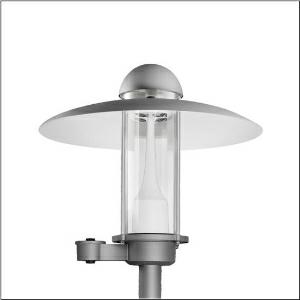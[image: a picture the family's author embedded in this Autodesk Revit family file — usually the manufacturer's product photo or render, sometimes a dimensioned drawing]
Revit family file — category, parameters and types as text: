
# Revit family: city-light_elegance_iq___st1_2a_5xa5265eu14h000022_aff6
name_source: partatom
category: Lighting Fixtures
units: mm (PartAtom-declared; Revit-internal decimal feet)

## family parameters
Cut with Voids When Loaded = No
Host = Face
Light Source = No
Part Type = Normal
Room Calculation Point = No
Round Connector Dimension = Use Diameter
Shared = No

## types (1)
- --- (1 x LED, 1460 lm, 10.7 W, 3000K)
    Apparent Load = 11 VA
    CIE Flux Codes = 22 62 94 98 100
    Color Rendering = 70
    Color Temperature = 3000K
    Default Elevation = 1800 mm
    Description = City-Light Elegance iQ, mast luminaire, Module 540 iQ-SR, primary light control with 3 zone facetted reflector, of plastic, silver coated, highly specular, structured, primary optical cover: cover, of PMMA, transparent, light distribution: ST1.2a, light emission: direct distribution, primary light characteristic: asymmetric, installation type: post-top, LED, High Power LED, rated luminous flux: 1.460lm, luminous efficacy: 136lm/W, light colour: 730, colour temperature: 3000K, control gear: iQ-Street Remote, D4i with power reduction, control: optimised constant luminous flux control (CLO 2.0), Desk-Remote (wireless, voltage-free reading and setting of iQ features in the workshop via application-optimized NFC function/RFID function), Light-Fading, Smart-Wire, Night-Set, Lumen-Switch, Temp-Guard, Auto-Match, Street-Remote, pre-setting: logarithmic dimming characteristic, with terminal, 6-pole, max. 2.5mm², mains connection: 230..240V, AC, 50/60Hz, connection cable pre-assembled, cable length: 5,5m, wiring characteristics: H07RN-F, start of lifetime: 11W, end of service life: 11W, reduction: 6W, luminaire housing, upper part, of aluminium, coated, Siteco® metallic grey (DB 702S), diameter: 750mm, height: 675mm, spigot size: d x l = 76 x 70mm (post-top) | with reducer (optional accessory) 60 x 70mm, mounting height: 3..5m, post-top mast mounting element, of diecast aluminium, coated, Siteco® metallic grey (DB 702S), Module 540 iQ-SR, traffic white (RAL 9016), equipment: standard, Smart Interface below, protection rating (complete): IP65, insulation class (complete): insulation class II (safety insulation), certification: CE, ENEC, VDE, packaging unit: 1 piece

Light Distribution: ST1.2a
    Height = 675 mm
    Lamp = 1 x LED
    Lamp Light Flux = 1460 lm
    Lamp Power = 10.7 W
    Lamp count = 1
    Length = 750 mm
    Luminous efficacy = 136 lm/W
    Manufacturer = Siteco
    ModVariant = No
    Model = 5XA5265EU14H000022
    Number of Poles = 1
    OnlyDefault = Yes
    Power Factor = 1
    Product Name = City-Light Elegance iQ | ST1.2a
    Product group = mast luminaire | pylon top
    ProductGroupID = 6100
    Protection Class = Protection class II
    Protection Degree = IP 65
    RLX_Detail_Level = 1
    RLX_Emergency_Light_Flux = 0 lm
    RLX_Emergency_Type = 0
    RLX_Emergency_Type_DB = No
    RlxData = <blob elided: 72681 chars, md5=8564df65>
    Socket = socket
    Standby Power = 0 W
    System Light Flux = 1460 lm
    System Power = 11 W
    Type Comments = factory setting: luminous flux: 100 % | dim-lin: 254 | 419 mA
    Type Image = l_1005991.jpg
    URL = http://relux.com
    VarID = @adj_107941
    Voltage = 0 V
    Weight = 0.00 kg
    Width = 0 mm  [stored 0 ft]

note: [stored X ft] marks values corroborated as IEEE doubles in the binary element streams (Revit-internal decimal feet)

## geometry (parser evidence)
native form markers: Blend x4, Sweep x10
no freeform markers — native parametric forms only
